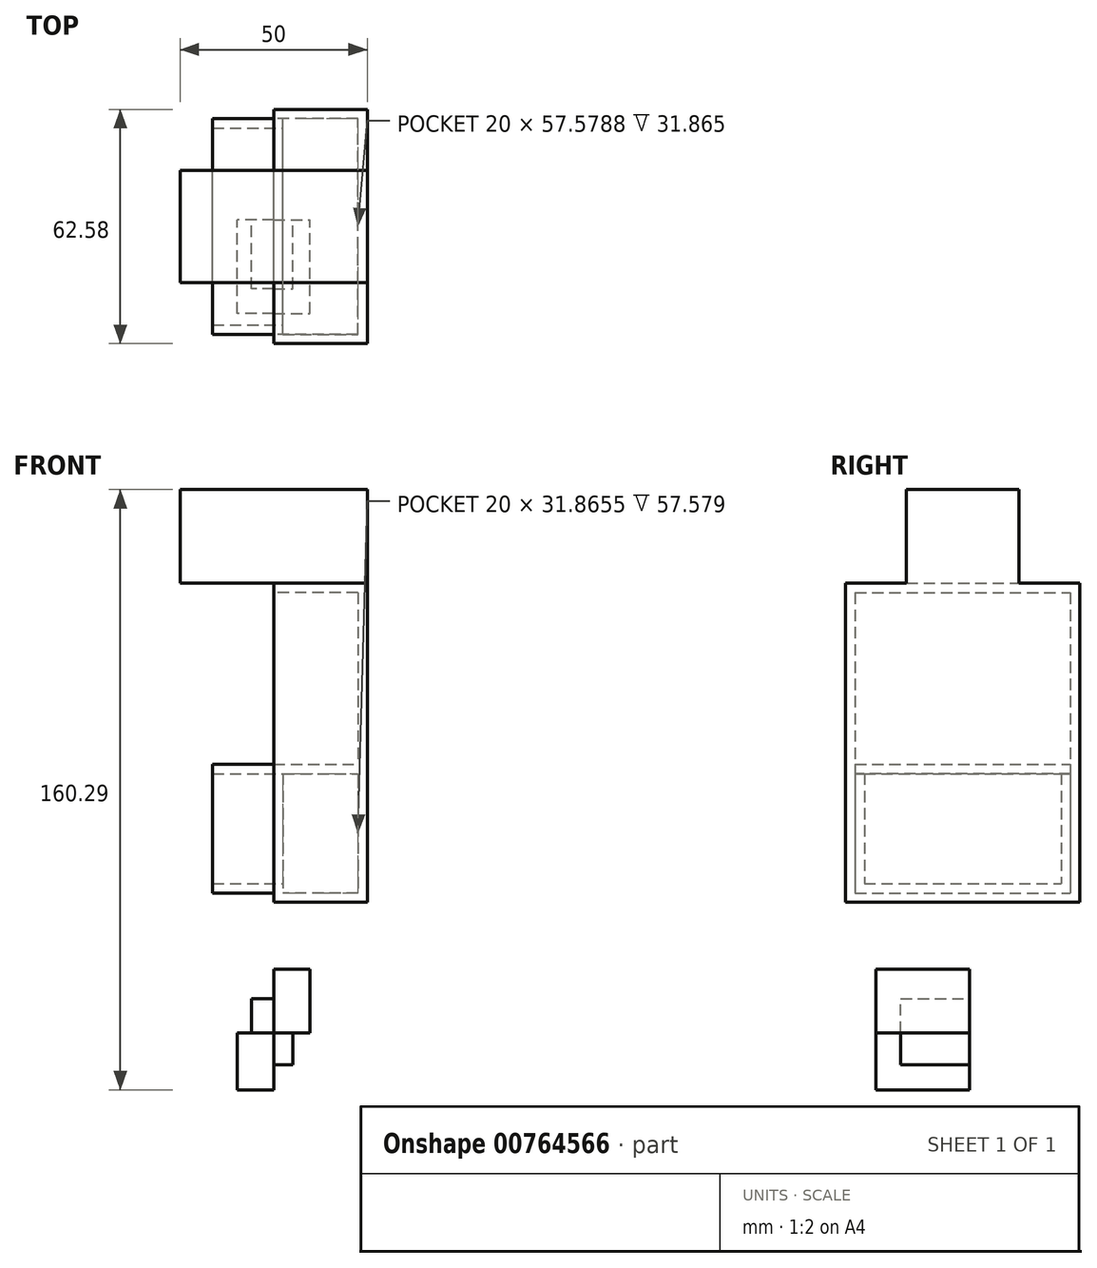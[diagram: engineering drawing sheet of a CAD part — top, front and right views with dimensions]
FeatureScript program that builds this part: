
annotation { "Feature Type Name" : "Feature", "Feature Type Description" : "" }
export const myFeature = defineFeature(function(context is Context, id is Id, definition is map)
    precondition{}
    {
        {
            var Q0;
            Q0=qCreatedBy(makeId("Front.planeOp"),FACE);
            var sketch = newSketch(context, id + "F0", { "sketchPlane" : qUnion([Q0])});
            skLineSegment(sketch, "E0.bottom", {"start": v(0, 0) * mm, "end": v(9.72, 0) * mm});
            skLineSegment(sketch, "E0.top", {"start": v(0, 17) * mm, "end": v(9.72, 17) * mm});
            skLineSegment(sketch, "E0.left", {"start": v(0, 0) * mm, "end": v(0, 17) * mm});
            skLineSegment(sketch, "E0.right", {"start": v(9.72, 0) * mm, "end": v(9.72, 17) * mm});
            skLineSegment(sketch, "E1.bottom", {"start": v(0, 0) * mm, "end": v(-9.72, 0) * mm});
            skLineSegment(sketch, "E1.top", {"start": v(0, -15.24) * mm, "end": v(-9.72, -15.24) * mm});
            skLineSegment(sketch, "E1.left", {"start": v(0, 0) * mm, "end": v(0, -15.24) * mm});
            skLineSegment(sketch, "E1.right", {"start": v(-9.72, 0) * mm, "end": v(-9.72, -15.24) * mm});
            skLineSegment(sketch, "E2.bottom", {"start": v(0, 0) * mm, "end": v(5.08, 0) * mm});
            skLineSegment(sketch, "E2.top", {"start": v(0, -8.62) * mm, "end": v(5.08, -8.62) * mm});
            skLineSegment(sketch, "E2.left", {"start": v(0, 0) * mm, "end": v(0, -8.62) * mm});
            skLineSegment(sketch, "E2.right", {"start": v(5.08, 0) * mm, "end": v(5.08, -8.62) * mm});
            skLineSegment(sketch, "E3.bottom", {"start": v(0, 0) * mm, "end": v(-5.96, 0) * mm});
            skLineSegment(sketch, "E3.top", {"start": v(0, 9.06) * mm, "end": v(-5.96, 9.06) * mm});
            skLineSegment(sketch, "E3.left", {"start": v(0, 0) * mm, "end": v(0, 9.06) * mm});
            skLineSegment(sketch, "E3.right", {"start": v(-5.96, 0) * mm, "end": v(-5.96, 9.06) * mm});
            skSolve(sketch);
        }
        {
            var Q0;
            {var subQ4=sQuery(id+"F0.wireOp",EDGE,"E0.top");Q0=makeQuery(id+"F0.imprint","IMPRINT",FACE,{"disambiguationData":[TD([[makeQuery(id+"F0.imprint","IMPRINT",EDGE,{"derivedFrom":subQ4}),-1.0]])]});}
            var Q1;
            {var subQ4=sQuery(id+"F0.wireOp",EDGE,"E1.top");Q1=makeQuery(id+"F0.imprint","IMPRINT",FACE,{"disambiguationData":[TD([[makeQuery(id+"F0.imprint","IMPRINT",EDGE,{"derivedFrom":subQ4}),-1.0]])]});}
            extrude(context, id + "F1", {"entities" : qUnion([Q0, Q1]), "depth" : 25 * mm, "offsetDistance" : 25 * mm});
        }
        {
            var Q0;
            {var subQ3=sQuery(id+"F0.wireOp",EDGE,"E3.top");Q0=makeQuery(id+"F0.imprint","IMPRINT",FACE,{"disambiguationData":[TD([[makeQuery(id+"F0.imprint","IMPRINT",EDGE,{"derivedFrom":subQ3}),1.0]])]});}
            var Q1;
            {var subQ4=sQuery(id+"F0.wireOp",EDGE,"E2.top");Q1=makeQuery(id+"F0.imprint","IMPRINT",FACE,{"disambiguationData":[TD([[makeQuery(id+"F0.imprint","IMPRINT",EDGE,{"derivedFrom":subQ4}),1.0]])]});}
            extrude(context, id + "F2", {"entities" : qUnion([Q0, Q1]), "depth" : 18.4 * mm, "offsetDistance" : 25 * mm});
        }
        {
            var Q0;
            Q0=qCreatedBy(makeId("Right.planeOp"),FACE);
            var sketch = newSketch(context, id + "F3", { "sketchPlane" : qUnion([Q0])});
            skLineSegment(sketch, "E4.bottom", {"start": v(-33.1, 120.05) * mm, "end": v(29.49, 120.05) * mm});
            skLineSegment(sketch, "E4.top", {"start": v(-33.1, 34.84) * mm, "end": v(29.49, 34.84) * mm});
            skLineSegment(sketch, "E4.left", {"start": v(-33.1, 120.05) * mm, "end": v(-33.1, 34.84) * mm});
            skLineSegment(sketch, "E4.right", {"start": v(29.49, 120.05) * mm, "end": v(29.49, 34.84) * mm});
            skSolve(sketch);
        }
        {
            var Q0;
            Q0 = qSketchRegion(id + "F3", true);
            extrude(context, id + "F4", {"entities" : qUnion([Q0]), "depth" : 25 * mm, "offsetDistance" : 25 * mm});
        }
        {
            var Q0;
            Q0=makeQuery(id+"F4.opExtrude","CAP_FACE",FACE,{"disambiguationData":[OSD([sQuery(id+"F3.wireOp",EDGE,"E4.bottom"),sQuery(id+"F3.wireOp",EDGE,"E4.top"),sQuery(id+"F3.wireOp",EDGE,"E4.left"),sQuery(id+"F3.wireOp",EDGE,"E4.right")])],"isStart":true});
            shell(context, id + "F5", {"entities" : qUnion([Q0]), "thickness" : 2.5 * mm});
        }
        {
            var Q0;
            Q0=makeQuery(id+"F5.opShell","OFFSET_FACE",FACE,{"disambiguationData":[OSD([sQuery(id+"F3.wireOp",EDGE,"E4.bottom"),sQuery(id+"F3.wireOp",EDGE,"E4.top"),sQuery(id+"F3.wireOp",EDGE,"E4.left"),sQuery(id+"F3.wireOp",EDGE,"E4.right")])]});
            var sketch = newSketch(context, id + "F6", { "sketchPlane" : qUnion([Q0])});
            skLineSegment(sketch, "E5.bottom", {"start": v(30.6, 37.34) * mm, "end": v(-26.99, 37.34) * mm});
            skLineSegment(sketch, "E5.top", {"start": v(30.6, 71.7) * mm, "end": v(-26.99, 71.7) * mm});
            skLineSegment(sketch, "E5.left", {"start": v(30.6, 37.34) * mm, "end": v(30.6, 71.7) * mm});
            skLineSegment(sketch, "E5.right", {"start": v(-26.99, 37.34) * mm, "end": v(-26.99, 71.7) * mm});
            skSolve(sketch);
        }
        {
            var Q0;
            Q0 = qSketchRegion(id + "F6", true);
            extrude(context, id + "F7", {"entities" : qUnion([Q0]), "operationType" : NewBodyOperationType.ADD, "depth" : 38.8 * mm, "offsetDistance" : 25 * mm});
        }
        {
            var Q0;
            Q0=makeQuery(id+"F7.opExtrude","CAP_FACE",FACE,{"disambiguationData":[OSD([sQuery(id+"F6.wireOp",EDGE,"E5.bottom"),sQuery(id+"F6.wireOp",EDGE,"E5.top"),sQuery(id+"F6.wireOp",EDGE,"E5.left"),sQuery(id+"F6.wireOp",EDGE,"E5.right")])],"isStart":false});
            shell(context, id + "F8", {"entities" : qUnion([Q0]), "thickness" : 2.5 * mm});
        }
        {
            var Q0;
            Q0=makeQuery(id+"F4.opExtrude","SWEPT_FACE",FACE,{"disambiguationData":[OSD([sQuery(id+"F3.wireOp",EDGE,"E4.bottom")])]});
            var sketch = newSketch(context, id + "F9", { "sketchPlane" : qUnion([Q0])});
            skLineSegment(sketch, "E6.bottom", {"start": v(25, -1.8) * mm, "end": v(0, -1.8) * mm});
            skLineSegment(sketch, "E6.top", {"start": v(25, -16.8) * mm, "end": v(0, -16.8) * mm});
            skLineSegment(sketch, "E6.left", {"start": v(25, -1.8) * mm, "end": v(25, -16.8) * mm});
            skLineSegment(sketch, "E6.right", {"start": v(0, -1.8) * mm, "end": v(0, -16.8) * mm});
            skLineSegment(sketch, "E7.top", {"start": v(25, 13.2) * mm, "end": v(0, 13.2) * mm});
            skLineSegment(sketch, "E7.left", {"start": v(25, -1.8) * mm, "end": v(25, 13.2) * mm});
            skLineSegment(sketch, "E7.right", {"start": v(0, -1.8) * mm, "end": v(0, 13.2) * mm});
            skSolve(sketch);
        }
        {
            var Q0;
            Q0 = qSketchRegion(id + "F9", true);
            extrude(context, id + "F10", {"entities" : qUnion([Q0]), "operationType" : NewBodyOperationType.ADD, "depth" : 25 * mm, "offsetDistance" : 25 * mm});
        }
        {
            var Q0;
            Q0=makeQuery(id+"F10.boolean.opBoolean","MERGE",FACE,{"derivedFrom":[makeQuery(id+"F4.opExtrude","CAP_FACE",FACE,{"disambiguationData":[OSD([sQuery(id+"F3.wireOp",EDGE,"E4.bottom"),sQuery(id+"F3.wireOp",EDGE,"E4.top"),sQuery(id+"F3.wireOp",EDGE,"E4.left"),sQuery(id+"F3.wireOp",EDGE,"E4.right")])],"isStart":true}),makeQuery(id+"F10.opExtrude","SWEPT_FACE",FACE,{"disambiguationData":[OSD([sQuery(id+"F9.wireOp",EDGE,"E6.right"),sQuery(id+"F9.wireOp",EDGE,"E7.right")])]})]});
            var sketch = newSketch(context, id + "F11", { "sketchPlane" : qUnion([Q0])});
            skLineSegment(sketch, "E8.bottom", {"start": v(16.8, 145.05) * mm, "end": v(-13.2, 145.05) * mm});
            skLineSegment(sketch, "E8.top", {"start": v(16.8, 120.05) * mm, "end": v(-13.2, 120.05) * mm});
            skLineSegment(sketch, "E8.left", {"start": v(16.8, 145.05) * mm, "end": v(16.8, 120.05) * mm});
            skLineSegment(sketch, "E8.right", {"start": v(-13.2, 145.05) * mm, "end": v(-13.2, 120.05) * mm});
            skSolve(sketch);
        }
        {
            var Q0;
            Q0 = qSketchRegion(id + "F11", true);
            extrude(context, id + "F12", {"entities" : qUnion([Q0]), "operationType" : NewBodyOperationType.ADD, "depth" : 25 * mm, "offsetDistance" : 25 * mm});
        }
    });
